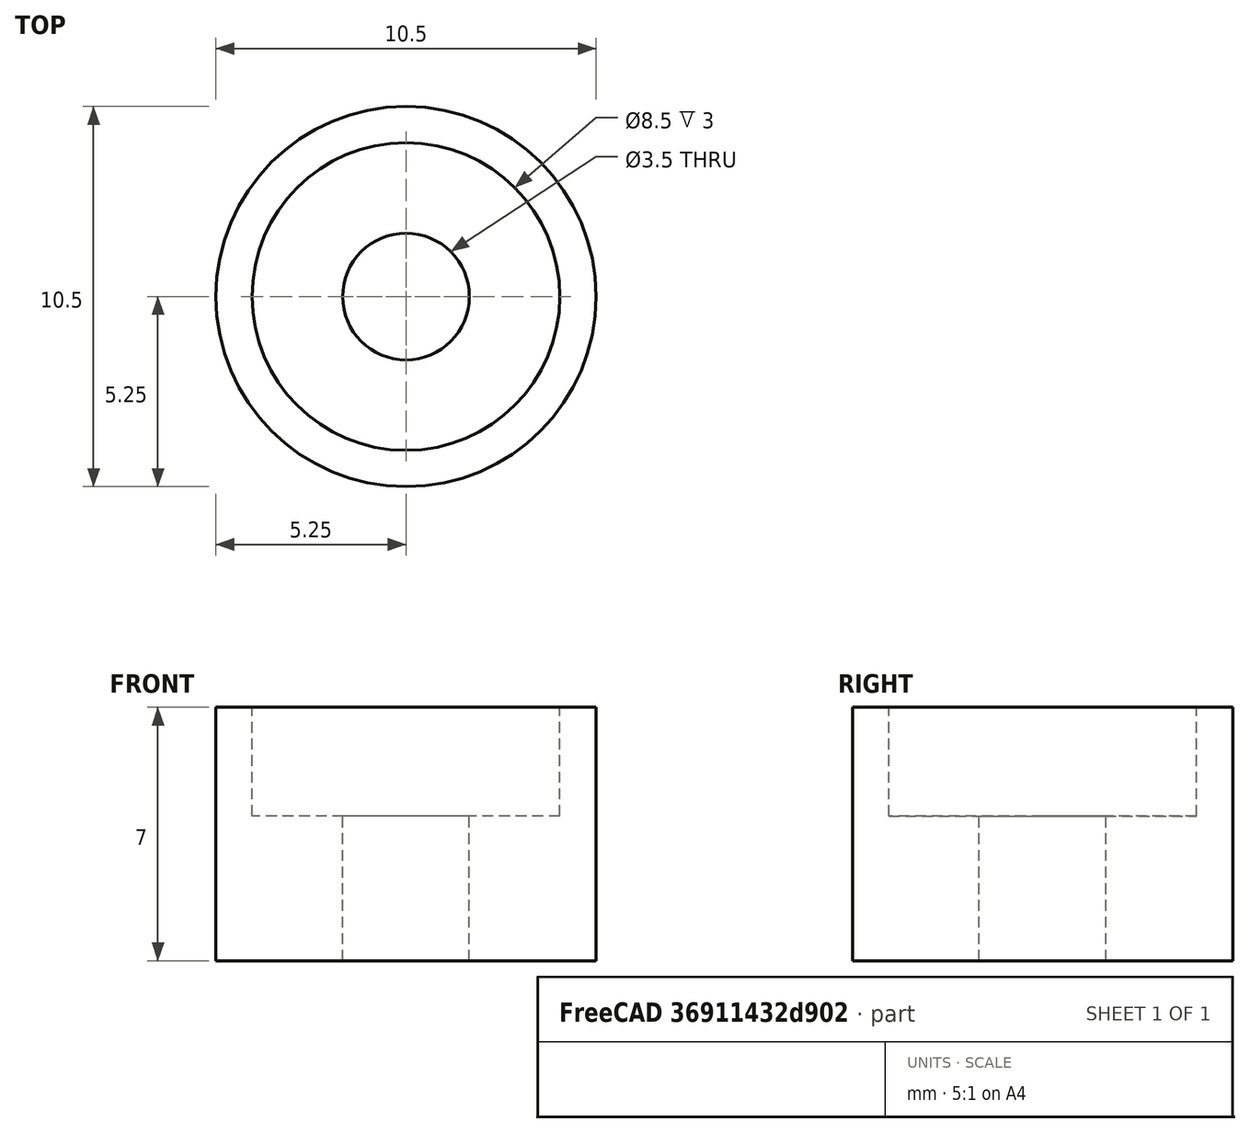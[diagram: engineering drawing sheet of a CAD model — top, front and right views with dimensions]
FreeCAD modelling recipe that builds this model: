
FCSTD DOCUMENT  (FreeCAD 0.21R33694 (Git))
Label: kirigami_bed_spacer
License: All rights reserved
LicenseURL: http://en.wikipedia.org/wiki/All_rights_reserved
objects: Spreadsheet::Sheet×1, Sketcher::SketchObject×1, PartDesign::Revolution×1, PartDesign::Body×1
note: 4 computed .brp shape members not serialized (recipe doc carries the construction recipe); baked Part::Feature solids carry a one-line shape summary decoded from their .brp

FEATURE [Spreadsheet::Sheet] Spreadsheet  label="settings"
  cells = A1='Setting; B1='mm; A2='Spring diameter; B2(dia_spring)=8.5; A3='Spring skirt thickness; B3(thi_skirt)=3; A4='Wall thickness; B4(thi_wall)=1; A5='Thickness; B5(thi_spacer)=4; A6='Hole Diameter; B6(dia_hole)=3.5; A8='Calculations; A9='Total diameter; B9(dia_total)==dia_spring + thi_wall * 2; A10='total height; B10(thi_total)==thi_spacer + thi_skirt
FEATURE [Sketcher::SketchObject] Sketch
  FullyConstrained = true
  MapMode = 5
  Placement = pos=(0,0,0) rot=(1,0,0;1.5708rad)
  Support = -> [XZ_Plane]
  expr: Constraints[11] = <<settings>>.dia_hole / 2
  expr: Constraints[23] = <<settings>>.thi_spacer
  expr: Constraints[24] = <<settings>>.thi_skirt
  expr: Constraints[25] = <<settings>>.dia_spring / 2
  expr: Constraints[26] = <<settings>>.thi_wall
  sketch-geometry (10):
    g0: LineSegment StartX=0 StartY=0 StartZ=0 EndX=5.25 EndY=0 EndZ=0
    g1: LineSegment StartX=5.25 StartY=0 StartZ=0 EndX=5.25 EndY=7 EndZ=0
    g2: LineSegment StartX=5.25 StartY=7 StartZ=0 EndX=0 EndY=7 EndZ=0
    g3: LineSegment StartX=0 StartY=7 StartZ=0 EndX=0 EndY=0 EndZ=0
    g4: LineSegment StartX=1.75 StartY=0 StartZ=0 EndX=5.25 EndY=0 EndZ=0
    g5: LineSegment StartX=1.75 StartY=0 StartZ=0 EndX=1.75 EndY=4 EndZ=0
    g6: LineSegment StartX=1.75 StartY=4 StartZ=0 EndX=4.25 EndY=4 EndZ=0
    g7: LineSegment StartX=4.25 StartY=4 StartZ=0 EndX=4.25 EndY=7 EndZ=0
    g8: LineSegment StartX=5.25 StartY=7 StartZ=0 EndX=4.25 EndY=7 EndZ=0
    g9: LineSegment StartX=5.25 StartY=7 StartZ=0 EndX=5.25 EndY=0 EndZ=0
  constraints (27):
    c: Coincident(g0,g1)
    c: Coincident(g1,g2)
    c: Coincident(g2,g3)
    c: Coincident(g3,g0)
    c: Horizontal(g0)
    c: Horizontal(g2)
    c: Vertical(g1)
    c: Vertical(g3)
    c: Coincident(g0,g-1)
    c: PointOnObject(g4,g0)
    c: Coincident(g4,g0)
    c: Distance(g0,g4) = 1.75
    c: Coincident(g5,g4)
    c: Vertical(g5)
    c: Coincident(g6,g5)
    c: Horizontal(g6)
    c: Coincident(g7,g6)
    c: PointOnObject(g7,g2)
    c: Vertical(g7)
    c: Coincident(g8,g1)
    c: Coincident(g8,g7)
    c: Coincident(g9,g8)
    c: Coincident(g9,g4)
    c: Distance(g5) = 4
    c: Distance(g7) = 3
    c: Distance(g6,g3) = 4.25
    c: Distance(g7,g8) = 1
FEATURE [PartDesign::Revolution] Revolution
  Angle = 360
  Axis = (0,-2e-16,1)
  Base = (0,0,0)
  Placement = pos=(0,0,0) rot=(1,0,0;1.5708rad)
  Profile = -> Sketch
  ReferenceAxis = -> Sketch [V_Axis]
  Reversed = true
FEATURE [PartDesign::Body] Body  label="bed_spacer"
  Group = -> [Sketch,Revolution]
  Origin = -> Origin
  Tip = -> Revolution
